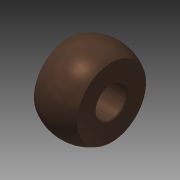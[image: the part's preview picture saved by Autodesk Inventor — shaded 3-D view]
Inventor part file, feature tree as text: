
AUTODESK INVENTOR PART (.ipt)
format: ipt  version: 2014 (Build 180170000, 170)  size: 117,760 bytes
history: native  units: in
note: dims shown in document units (in); Inventor stores cm internally (conversion verified against a paired STEP export)
features: sketch x2, revolve x1, hole x1, chamfer x1
ambient origin geometry x8: Origin, YZ Plane, XZ Plane, XY Plane, X Axis, Y Axis, Z Axis, Center Point
bodies: Solid1 (feature_tree)
feature tree (5):
  revolve  "Revolution1"  [1 undecoded]
  hole  "Hole1"  [1 undecoded]
  chamfer  "Chamfer1"  Distance=0.01in Angle=45.0deg
  sketch  "Sketch1"  dims[d44=0.852in d45=0.5in]
  sketch  "Sketch2"  dims[d46=0.5in d47=90.0deg d48=0.3755in d49=0.75in d50=0.375in d51=0.25in d52=0.5635in d53=1.0in d54=0.8108in d55=0.01in d56=0.125in d57=45.0deg]
note: 2 required parameter values undecoded (feature->parameter linkage not recoverable at this tier; creation-order binding heuristic only, values carry confidence <= 0.55)